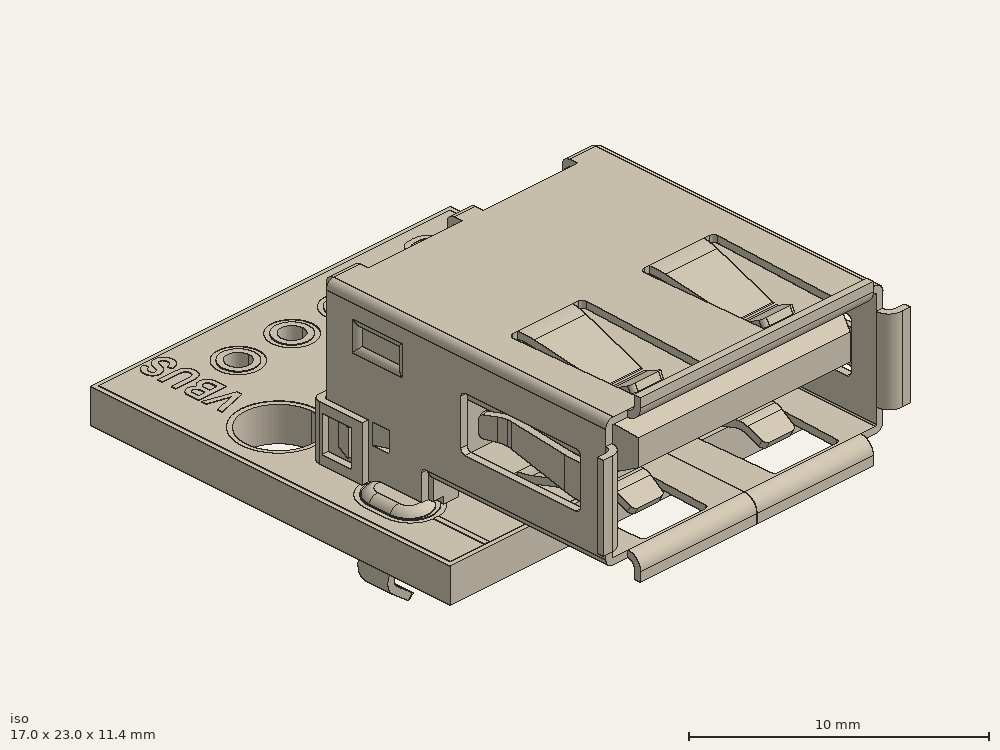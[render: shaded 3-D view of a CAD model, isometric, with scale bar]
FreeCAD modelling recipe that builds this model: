
FCSTD DOCUMENT  (FreeCAD 0.20R29177 (Git))
Label: usbFem_001
License: All rights reserved
LicenseURL: http://en.wikipedia.org/wiki/All_rights_reserved
objects: Sketcher::SketchObject×3, Part::Feature×1, Spreadsheet::Sheet×1, PartDesign::Body×1, App::Part×1
note: 5 computed .brp shape members not serialized (recipe doc carries the construction recipe); baked Part::Feature solids carry a one-line shape summary decoded from their .brp

FEATURE [Part::Feature] Part__Feature  label="WR-COM USB 2.0 Type A Horizontal THT_614004190021 (rev1)"
  shape: bbox 17.01 x 23.01 x 11.41 mm, 3609 faces, 48 solids (baked)
FEATURE [Sketcher::SketchObject] Sketch  label="planHrzSk"
  FullyConstrained = false
  MapMode = 5
  Support = -> [XY_Plane001]
  sketch-geometry (7):
    g0: LineSegment StartX=-8.53525 StartY=11.5508 StartZ=0 EndX=8.49801 EndY=11.5508 EndZ=0
    g1: LineSegment StartX=8.49801 StartY=11.5508 StartZ=0 EndX=8.49801 EndY=-5.4299 EndZ=0
    g2: LineSegment StartX=8.49801 StartY=-5.4299 StartZ=0 EndX=-8.53525 EndY=-5.4299 EndZ=0
    g3: LineSegment StartX=-8.53525 StartY=-5.4299 StartZ=0 EndX=-8.53525 EndY=11.5508 EndZ=0
    g4: Circle CenterX=-6.00841 CenterY=5.14787 CenterZ=0 NormalX=0 NormalY=0 NormalZ=1 AngleXU=0 Radius=1.6
    g5: Circle CenterX=6.00841 CenterY=5.14787 CenterZ=0 NormalX=0 NormalY=0 NormalZ=1 AngleXU=0 Radius=1.6
    g6: LineSegment StartX=-6.00841 StartY=5.14787 StartZ=0 EndX=6.00841 EndY=5.14787 EndZ=0
  constraints (18):
    c: Coincident(g0,g1)
    c: Coincident(g1,g2)
    c: Coincident(g2,g3)
    c: Coincident(g3,g0)
    c: Horizontal(g0)
    c: Horizontal(g2)
    c: Vertical(g1)
    c: Vertical(g3)
    c: DistanceX(g0,g0) = 17.0333
    c: DistanceY(g3,g3) = 16.9807
    c: Coincident(g6,g4)
    c: Coincident(g6,g5)
    c: Equal(g5,g4)
    c: Diameter(g5) = 3.2
    c: DistanceX(g6,g6) = 12.0168
    c: DistanceY(g2,g4) = 10.5778
    c: Symmetric(g4,g5,g-2)
    c: DistanceY(g4,g0) = 6.40292
FEATURE [Sketcher::SketchObject] Sketch001  label="planVertProfilSk"
  FullyConstrained = false
  MapMode = 5
  Placement = pos=(0,0,0) rot=(0.57735,0.57735,0.57735;2.0944rad)
  Support = -> [YZ_Plane001]
  sketch-geometry (8):
    g0: LineSegment StartX=-10.8262 StartY=6.75736 StartZ=0 EndX=2.94928 EndY=6.75736 EndZ=0
    g1: LineSegment StartX=2.94928 StartY=6.75736 StartZ=0 EndX=2.94928 EndY=-1.54264 EndZ=0
    g2: LineSegment StartX=2.94928 StartY=-1.54264 StartZ=0 EndX=-10.8262 EndY=-1.54264 EndZ=0
    g3: LineSegment StartX=-10.8262 StartY=-1.54264 StartZ=0 EndX=-10.8262 EndY=6.75736 EndZ=0
    g4: LineSegment StartX=11.5493 StartY=-1.54264 StartZ=0 EndX=2.94928 EndY=-1.54264 EndZ=0
    g5: LineSegment StartX=2.94928 StartY=-1.54264 StartZ=0 EndX=2.94928 EndY=6.75736 EndZ=0
    g6: LineSegment StartX=2.94928 StartY=6.75736 StartZ=0 EndX=11.5493 EndY=6.75736 EndZ=0
    g7: LineSegment StartX=11.5493 StartY=6.75736 StartZ=0 EndX=11.5493 EndY=-1.54264 EndZ=0
  constraints (19):
    c: Coincident(g0,g1)
    c: Coincident(g1,g2)
    c: Coincident(g2,g3)
    c: Coincident(g3,g0)
    c: Horizontal(g0)
    c: Horizontal(g2)
    c: Vertical(g1)
    c: Vertical(g3)
    c: Coincident(g4,g5)
    c: Coincident(g5,g6)
    c: Coincident(g6,g7)
    c: Coincident(g7,g4)
    c: Horizontal(g4)
    c: Horizontal(g6)
    c: Vertical(g7)
    c: Coincident(g5,g0)
    c: DistanceY(g7,g7) = 8.3
    c: DistanceX(g6,g6) = 8.6
    c: Coincident(g1,g4)
FEATURE [Spreadsheet::Sheet] Spreadsheet  label="usbFemSp"
  cells = A2=trousEntraxe; B2(trousEntraxe)=12; A3=trousBordSupDist; B3(trousBordSupDist)=6.4; A4=trousDiam; B4(trousDiam)=3.2; A5=fentreLong; B5(fentreLong)=13.7; C5=13.2 mesurée + 0.5 pour compensé l'impression; A6=fentreHaut; B6(fentreHaut)=6.3; C6=5.8+0.5; A7=fenetreBasePSBTopDist; B7(fenetreBasePSBTopDist)=8.300000000000001
FEATURE [Sketcher::SketchObject] Sketch002  label="planVertFaceSk"
  FullyConstrained = false
  MapMode = 5
  Placement = pos=(0,0,0) rot=(1,0,0;1.5708rad)
  Support = -> [XZ_Plane001]
  sketch-geometry (8):
    g0: LineSegment StartX=-8.51172 StartY=-1.47776 StartZ=0 EndX=8.51172 EndY=-1.47776 EndZ=0
    g1: LineSegment StartX=8.51172 StartY=-1.47776 StartZ=0 EndX=8.51172 EndY=6.84754 EndZ=0
    g2: LineSegment StartX=8.51172 StartY=6.84754 StartZ=0 EndX=-8.51172 EndY=6.84754 EndZ=0
    g3: LineSegment StartX=-8.51172 StartY=6.84754 StartZ=0 EndX=-8.51172 EndY=-1.47776 EndZ=0
    g4: LineSegment StartX=-6.61961 StartY=6.84754 StartZ=0 EndX=6.61961 EndY=6.84754 EndZ=0
    g5: LineSegment StartX=6.61961 StartY=6.84754 StartZ=0 EndX=6.61961 EndY=1.2658 EndZ=0
    g6: LineSegment StartX=6.61961 StartY=1.2658 StartZ=0 EndX=-6.61961 EndY=1.2658 EndZ=0
    g7: LineSegment StartX=-6.61961 StartY=1.2658 StartZ=0 EndX=-6.61961 EndY=6.84754 EndZ=0
  constraints (19):
    c: Coincident(g0,g1)
    c: Coincident(g1,g2)
    c: Coincident(g2,g3)
    c: Coincident(g3,g0)
    c: Horizontal(g0)
    c: Vertical(g1)
    c: Vertical(g3)
    c: Coincident(g4,g5)
    c: Coincident(g5,g6)
    c: Coincident(g6,g7)
    c: Coincident(g7,g4)
    c: Horizontal(g6)
    c: Vertical(g5)
    c: Vertical(g7)
    c: PointOnObject(g4,g2)
    c: DistanceX(g4,g4) = 13.2392
    c: Symmetric(g4,g4,g-2)
    c: Symmetric(g2,g1,g-2)
    c: DistanceY(g6,g4) = 5.58173
FEATURE [PartDesign::Body] Body  label="checkerBdy"
  Group = -> [Sketch,Sketch001,Sketch002]
  Origin = -> Origin001
FEATURE [App::Part] Part  label="usbFemBBPart"
  Group = -> [Part__Feature,Body,Spreadsheet]
  Origin = -> Origin
